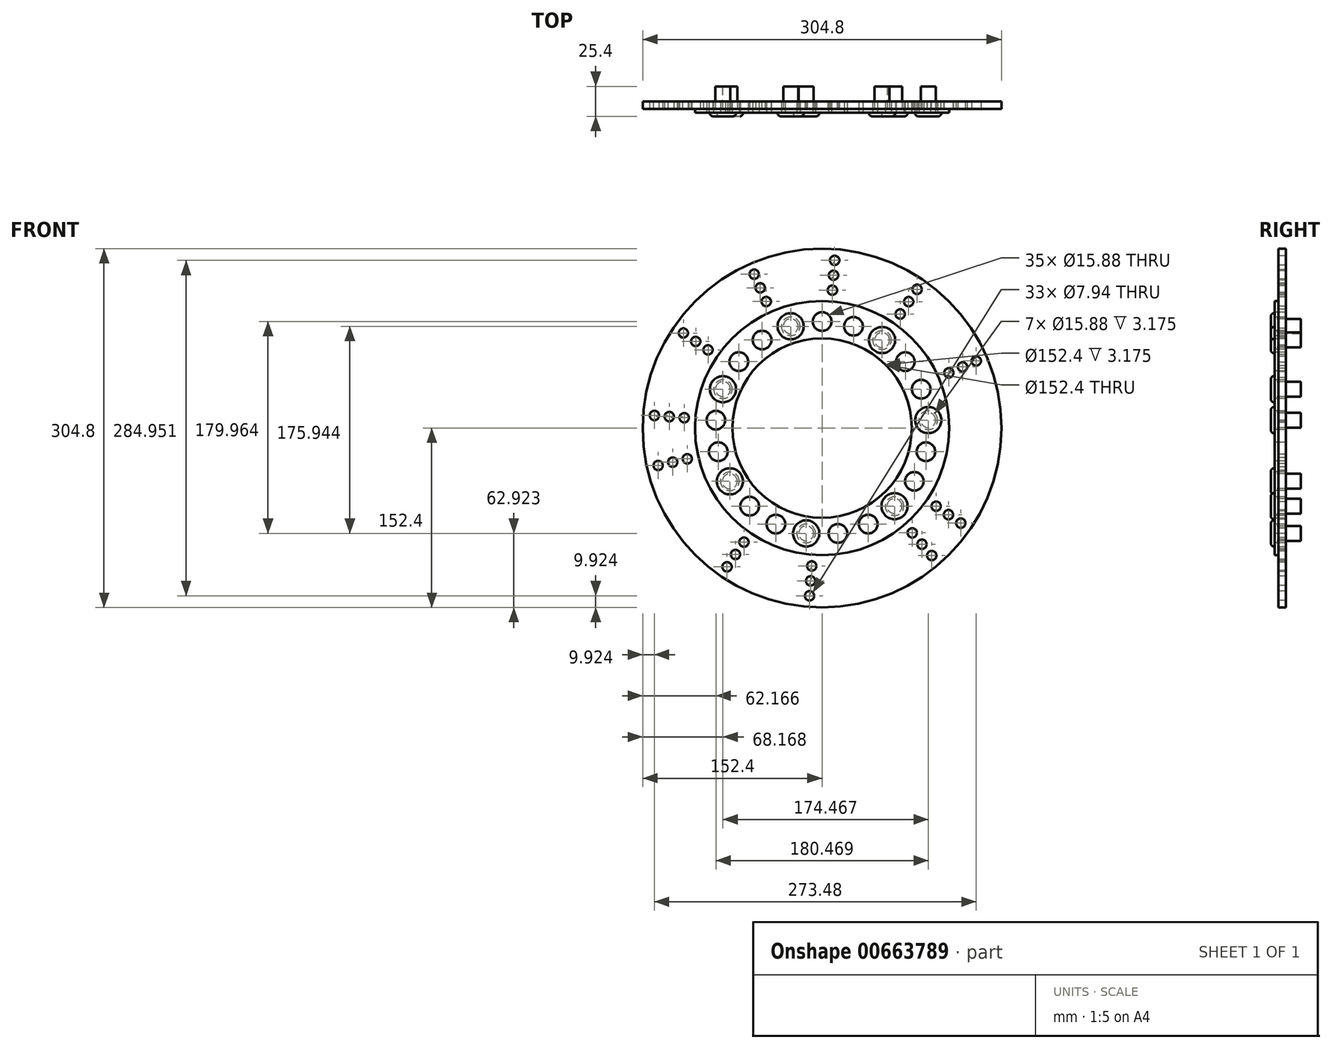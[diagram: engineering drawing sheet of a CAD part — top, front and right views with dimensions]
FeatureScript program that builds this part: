
annotation { "Feature Type Name" : "Feature", "Feature Type Description" : "" }
export const myFeature = defineFeature(function(context is Context, id is Id, definition is map)
    precondition{}
    {
        {
            var Q0;
            Q0=qCreatedBy(makeId("Front.planeOp"),FACE);
            var sketch = newSketch(context, id + "F0", { "sketchPlane" : qUnion([Q0])});
            skCircle(sketch, "E0", {"center": v(0, 0) * mm, "radius": 152.4 * mm});
            skCircle(sketch, "E1", {"center": v(0, 0) * mm, "radius": 76.2 * mm});
            skSolve(sketch);
        }
        {
            var Q0;
            Q0 = qSketchRegion(id + "F0", true);
            extrude(context, id + "F1", {"entities" : qUnion([Q0]), "depth" : 6.35 * mm, "offsetDistance" : 25.4 * mm});
        }
        {
            var Q0;
            Q0=makeQuery(id+"F1.opExtrude","CAP_FACE",FACE,{"disambiguationData":[OSD([sQuery(id+"F0.wireOp",EDGE,"E0"),sQuery(id+"F0.wireOp",EDGE,"E1")])],"isStart":false});
            var sketch = newSketch(context, id + "F2", { "sketchPlane" : qUnion([Q0])});
            skCircle(sketch, "E2", {"center": v(0, 0) * mm, "radius": 76.2 * mm});
            skCircle(sketch, "E3", {"center": v(0, 0) * mm, "radius": 107.95 * mm});
            skSolve(sketch);
        }
        {
            var Q0;
            Q0 = qSketchRegion(id + "F2", true);
            extrude(context, id + "F3", {"entities" : qUnion([Q0]), "depth" : 3.17 * mm, "offsetDistance" : 25.4 * mm});
        }
        {
            var Q0;
            Q0=makeQuery(id+"F3.opExtrude","CAP_FACE",FACE,{"disambiguationData":[OSD([sQuery(id+"F2.wireOp",EDGE,"E2"),sQuery(id+"F2.wireOp",EDGE,"E3")])],"isStart":false});
            var sketch = newSketch(context, id + "F4", { "sketchPlane" : qUnion([Q0])});
            skCircle(sketch, "E4", {"center": v(0, 90.49) * mm, "radius": 7.94 * mm});
            skCircle(sketch, "E5.1.0", {"center": v(-26.67, 86.47) * mm, "radius": 7.94 * mm});
            skCircle(sketch, "E5.2.0", {"center": v(-50.97, 74.76) * mm, "radius": 7.94 * mm});
            skCircle(sketch, "E5.3.0", {"center": v(-70.75, 56.42) * mm, "radius": 7.94 * mm});
            skCircle(sketch, "E5.4.0", {"center": v(-84.23, 33.06) * mm, "radius": 7.94 * mm});
            skCircle(sketch, "E5.5.0", {"center": v(-90.23, 6.76) * mm, "radius": 7.94 * mm});
            skCircle(sketch, "E5.6.0", {"center": v(-88.22, -20.14) * mm, "radius": 7.94 * mm});
            skCircle(sketch, "E5.7.0", {"center": v(-78.36, -45.24) * mm, "radius": 7.94 * mm});
            skCircle(sketch, "E5.8.0", {"center": v(-61.55, -66.33) * mm, "radius": 7.94 * mm});
            skCircle(sketch, "E5.9.0", {"center": v(-39.26, -81.53) * mm, "radius": 7.94 * mm});
            skCircle(sketch, "E5.10.0", {"center": v(-13.49, -89.48) * mm, "radius": 7.94 * mm});
            skCircle(sketch, "E5.11.0", {"center": v(13.49, -89.48) * mm, "radius": 7.94 * mm});
            skCircle(sketch, "E5.12.0", {"center": v(39.26, -81.53) * mm, "radius": 7.94 * mm});
            skCircle(sketch, "E5.13.0", {"center": v(61.55, -66.33) * mm, "radius": 7.94 * mm});
            skCircle(sketch, "E5.14.0", {"center": v(78.36, -45.24) * mm, "radius": 7.94 * mm});
            skCircle(sketch, "E5.15.0", {"center": v(88.22, -20.14) * mm, "radius": 7.94 * mm});
            skCircle(sketch, "E5.16.0", {"center": v(90.23, 6.76) * mm, "radius": 7.94 * mm});
            skCircle(sketch, "E5.17.0", {"center": v(84.23, 33.06) * mm, "radius": 7.94 * mm});
            skCircle(sketch, "E5.18.0", {"center": v(70.75, 56.42) * mm, "radius": 7.94 * mm});
            skCircle(sketch, "E5.19.0", {"center": v(50.97, 74.76) * mm, "radius": 7.94 * mm});
            skPoint(sketch, "E5.center", {"position": v(0, 0) * mm});
            skCircle(sketch, "E6.1.20.0", {"center": v(26.67, 86.47) * mm, "radius": 7.94 * mm});
            skSolve(sketch);
        }
        {
            var Q0;
            Q0 = qSketchRegion(id + "F4", true);
            extrude(context, id + "F5", {"entities" : qUnion([Q0]), "operationType" : NewBodyOperationType.REMOVE, "endBound" : BoundingType.THROUGH_ALL, "oppositeDirection" : true, "depth" : 25.4 * mm, "offsetDistance" : 25.4 * mm});
        }
        {
            var Q0;
            Q0=makeQuery(id+"F3.opExtrude","CAP_FACE",FACE,{"disambiguationData":[OSD([sQuery(id+"F2.wireOp",EDGE,"E2"),sQuery(id+"F2.wireOp",EDGE,"E3")])],"isStart":false});
            var sketch = newSketch(context, id + "F6", { "sketchPlane" : qUnion([Q0])});
            skCircle(sketch, "E7", {"center": v(-13.49, -89.48) * mm, "radius": 11.11 * mm});
            skCircle(sketch, "E8", {"center": v(-78.36, -45.24) * mm, "radius": 11.11 * mm});
            skCircle(sketch, "E9", {"center": v(-84.23, 33.06) * mm, "radius": 11.11 * mm});
            skCircle(sketch, "E10", {"center": v(-26.67, 86.47) * mm, "radius": 11.11 * mm});
            skCircle(sketch, "E11", {"center": v(50.97, 74.76) * mm, "radius": 11.11 * mm});
            skCircle(sketch, "E12", {"center": v(90.23, 6.76) * mm, "radius": 11.11 * mm});
            skCircle(sketch, "E13", {"center": v(61.55, -66.33) * mm, "radius": 11.11 * mm});
            skSolve(sketch);
        }
        {
            var Q0;
            Q0 = qSketchRegion(id + "F6", true);
            extrude(context, id + "F7", {"entities" : qUnion([Q0]), "operationType" : NewBodyOperationType.ADD, "depth" : 3.17 * mm, "offsetDistance" : 25.4 * mm});
        }
        {
            var Q0;
            Q0=makeQuery(id+"F1.opExtrude","CAP_FACE",FACE,{"disambiguationData":[OSD([sQuery(id+"F0.wireOp",EDGE,"E0"),sQuery(id+"F0.wireOp",EDGE,"E1")])],"isStart":false});
            var sketch = newSketch(context, id + "F8", { "sketchPlane" : qUnion([Q0])});
            skLineSegment(sketch, "E14", {"start": v(0, 107.95) * mm, "end": v(0, 152.4) * mm, "construction": true});
            skLineSegment(sketch, "E15", {"start": v(-7.94, 116.43) * mm, "end": v(7.94, 143.92) * mm, "construction": true});
            skCircle(sketch, "E16", {"center": v(0, 130.17) * mm, "radius": 3.97 * mm});
            skCircle(sketch, "E17", {"center": v(-7.94, 116.43) * mm, "radius": 3.97 * mm});
            skCircle(sketch, "E18", {"center": v(7.94, 143.92) * mm, "radius": 3.97 * mm});
            skCircle(sketch, "E19.1.0", {"center": v(-49.82, 120.27) * mm, "radius": 3.97 * mm});
            skCircle(sketch, "E19.1.1", {"center": v(-47.74, 136) * mm, "radius": 3.97 * mm});
            skCircle(sketch, "E19.1.2", {"center": v(-51.89, 104.53) * mm, "radius": 3.97 * mm});
            skCircle(sketch, "E19.2.0", {"center": v(-92.05, 92.05) * mm, "radius": 3.97 * mm});
            skCircle(sketch, "E19.2.1", {"center": v(-96.16, 107.38) * mm, "radius": 3.97 * mm});
            skCircle(sketch, "E19.2.2", {"center": v(-87.94, 76.71) * mm, "radius": 3.97 * mm});
            skCircle(sketch, "E19.3.0", {"center": v(-120.27, 49.82) * mm, "radius": 3.97 * mm});
            skCircle(sketch, "E19.3.1", {"center": v(-129.93, 62.41) * mm, "radius": 3.97 * mm});
            skCircle(sketch, "E19.3.2", {"center": v(-110.6, 37.22) * mm, "radius": 3.97 * mm});
            skCircle(sketch, "E19.4.0", {"center": v(-130.17, 0) * mm, "radius": 3.97 * mm});
            skCircle(sketch, "E19.4.1", {"center": v(-143.92, 7.94) * mm, "radius": 3.97 * mm});
            skCircle(sketch, "E19.4.2", {"center": v(-116.43, -7.94) * mm, "radius": 3.97 * mm});
            skCircle(sketch, "E19.5.0", {"center": v(-120.27, -49.82) * mm, "radius": 3.97 * mm});
            skCircle(sketch, "E19.5.1", {"center": v(-136, -47.74) * mm, "radius": 3.97 * mm});
            skCircle(sketch, "E19.5.2", {"center": v(-104.53, -51.89) * mm, "radius": 3.97 * mm});
            skCircle(sketch, "E19.6.0", {"center": v(-92.05, -92.05) * mm, "radius": 3.97 * mm});
            skCircle(sketch, "E19.6.1", {"center": v(-107.38, -96.16) * mm, "radius": 3.97 * mm});
            skCircle(sketch, "E19.6.2", {"center": v(-76.71, -87.94) * mm, "radius": 3.97 * mm});
            skCircle(sketch, "E19.7.0", {"center": v(-49.82, -120.27) * mm, "radius": 3.97 * mm});
            skCircle(sketch, "E19.7.1", {"center": v(-62.41, -129.93) * mm, "radius": 3.97 * mm});
            skCircle(sketch, "E19.7.2", {"center": v(-37.22, -110.6) * mm, "radius": 3.97 * mm});
            skCircle(sketch, "E19.8.0", {"center": v(0, -130.17) * mm, "radius": 3.97 * mm});
            skCircle(sketch, "E19.8.1", {"center": v(-7.94, -143.92) * mm, "radius": 3.97 * mm});
            skCircle(sketch, "E19.8.2", {"center": v(7.94, -116.43) * mm, "radius": 3.97 * mm});
            skCircle(sketch, "E19.9.0", {"center": v(49.82, -120.27) * mm, "radius": 3.97 * mm});
            skCircle(sketch, "E19.9.1", {"center": v(47.74, -136) * mm, "radius": 3.97 * mm});
            skCircle(sketch, "E19.9.2", {"center": v(51.89, -104.53) * mm, "radius": 3.97 * mm});
            skCircle(sketch, "E19.10.0", {"center": v(92.05, -92.05) * mm, "radius": 3.97 * mm});
            skCircle(sketch, "E19.10.1", {"center": v(96.16, -107.38) * mm, "radius": 3.97 * mm});
            skCircle(sketch, "E19.10.2", {"center": v(87.94, -76.71) * mm, "radius": 3.97 * mm});
            skCircle(sketch, "E19.11.0", {"center": v(120.27, -49.82) * mm, "radius": 3.97 * mm});
            skCircle(sketch, "E19.11.1", {"center": v(129.93, -62.41) * mm, "radius": 3.97 * mm});
            skCircle(sketch, "E19.11.2", {"center": v(110.6, -37.22) * mm, "radius": 3.97 * mm});
            skCircle(sketch, "E19.12.0", {"center": v(130.17, 0) * mm, "radius": 3.97 * mm});
            skCircle(sketch, "E19.12.1", {"center": v(143.92, -7.94) * mm, "radius": 3.97 * mm});
            skCircle(sketch, "E19.12.2", {"center": v(116.43, 7.94) * mm, "radius": 3.97 * mm});
            skCircle(sketch, "E19.13.0", {"center": v(120.27, 49.82) * mm, "radius": 3.97 * mm});
            skCircle(sketch, "E19.13.1", {"center": v(136, 47.74) * mm, "radius": 3.97 * mm});
            skCircle(sketch, "E19.13.2", {"center": v(104.53, 51.89) * mm, "radius": 3.97 * mm});
            skCircle(sketch, "E19.14.0", {"center": v(92.05, 92.05) * mm, "radius": 3.97 * mm});
            skCircle(sketch, "E19.14.1", {"center": v(107.38, 96.16) * mm, "radius": 3.97 * mm});
            skCircle(sketch, "E19.14.2", {"center": v(76.71, 87.94) * mm, "radius": 3.97 * mm});
            skCircle(sketch, "E19.15.0", {"center": v(49.82, 120.27) * mm, "radius": 3.97 * mm});
            skCircle(sketch, "E19.15.1", {"center": v(62.41, 129.93) * mm, "radius": 3.97 * mm});
            skCircle(sketch, "E19.15.2", {"center": v(37.22, 110.6) * mm, "radius": 3.97 * mm});
            skPoint(sketch, "E19.center", {"position": v(0, 0) * mm});
            skSolve(sketch);
        }
        {
            var Q0;
            Q0=makeQuery(id+"F7.opExtrude","CAP_FACE",FACE,{"disambiguationData":[OSD([sQuery(id+"F6.wireOp",EDGE,"E13")])],"isStart":false});
            var Q1;
            Q1=makeQuery(id+"F7.opExtrude","CAP_FACE",FACE,{"disambiguationData":[OSD([sQuery(id+"F6.wireOp",EDGE,"E7")])],"isStart":false});
            var Q2;
            Q2=makeQuery(id+"F7.opExtrude","CAP_FACE",FACE,{"disambiguationData":[OSD([sQuery(id+"F6.wireOp",EDGE,"E8")])],"isStart":false});
            var Q3;
            Q3=makeQuery(id+"F7.opExtrude","CAP_FACE",FACE,{"disambiguationData":[OSD([sQuery(id+"F6.wireOp",EDGE,"E9")])],"isStart":false});
            var Q4;
            Q4=makeQuery(id+"F7.opExtrude","CAP_FACE",FACE,{"disambiguationData":[OSD([sQuery(id+"F6.wireOp",EDGE,"E10")])],"isStart":false});
            var Q5;
            Q5=makeQuery(id+"F7.opExtrude","CAP_FACE",FACE,{"disambiguationData":[OSD([sQuery(id+"F6.wireOp",EDGE,"E11")])],"isStart":false});
            var Q6;
            Q6=makeQuery(id+"F7.opExtrude","CAP_FACE",FACE,{"disambiguationData":[OSD([sQuery(id+"F6.wireOp",EDGE,"E12")])],"isStart":false});
            fillet(context, id + "F9", {"entities" : qUnion([Q0, Q1, Q2, Q3, Q4, Q5, Q6]), "radius" : 2.54 * mm, "tangentPropagation" : true, "allowEdgeOverflow" : false});
        }
        {
            var Q0;
            Q0=makeQuery(id+"F7.opExtrude","CAP_FACE",FACE,{"disambiguationData":[OSD([sQuery(id+"F6.wireOp",EDGE,"E10")])],"isStart":false});
            var sketch = newSketch(context, id + "F10", { "sketchPlane" : qUnion([Q0])});
            skCircle(sketch, "E20", {"center": v(-26.67, 86.47) * mm, "radius": 6.35 * mm});
            skCircle(sketch, "E21.1.0", {"center": v(-84.23, 33.06) * mm, "radius": 6.35 * mm});
            skCircle(sketch, "E21.2.0", {"center": v(-78.36, -45.24) * mm, "radius": 6.35 * mm});
            skCircle(sketch, "E21.3.0", {"center": v(-13.49, -89.48) * mm, "radius": 6.35 * mm});
            skCircle(sketch, "E21.4.0", {"center": v(61.55, -66.33) * mm, "radius": 6.35 * mm});
            skCircle(sketch, "E21.5.0", {"center": v(90.23, 6.76) * mm, "radius": 6.35 * mm});
            skCircle(sketch, "E21.6.0", {"center": v(50.97, 74.76) * mm, "radius": 6.35 * mm});
            skPoint(sketch, "E21.center", {"position": v(0, 0) * mm});
            skSolve(sketch);
        }
        {
            var Q0;
            Q0 = qSketchRegion(id + "F10", true);
            extrude(context, id + "F11", {"entities" : qUnion([Q0]), "operationType" : NewBodyOperationType.ADD, "oppositeDirection" : true, "depth" : 25.4 * mm, "offsetDistance" : 25.4 * mm});
        }
        {
            var Q0;
            Q0=makeQuery(id+"F8.imprint","IMPRINT",FACE,{"disambiguationData":[TD([[makeQuery(id+"F8.imprint","IMPRINT",EDGE,{"derivedFrom":sQuery(id+"F8.wireOp",EDGE,"E16")}),-1.0]])]});
            var sketch = newSketch(context, id + "F12", { "sketchPlane" : qUnion([Q0])});
            skLineSegment(sketch, "E22", {"start": v(0, 0) * mm, "end": v(-57.68, 130.72) * mm, "construction": true});
            skLineSegment(sketch, "E23", {"start": v(0, 0) * mm, "end": v(-117.86, 80.77) * mm, "construction": true});
            skLineSegment(sketch, "E24", {"start": v(0, 0) * mm, "end": v(-142.48, 10.68) * mm, "construction": true});
            skLineSegment(sketch, "E25", {"start": v(0, 0) * mm, "end": v(-139.3, -31.8) * mm, "construction": true});
            skLineSegment(sketch, "E26", {"start": v(0, 0) * mm, "end": v(-80.77, -117.86) * mm, "construction": true});
            skLineSegment(sketch, "E27", {"start": v(0, 0) * mm, "end": v(-10.68, -142.48) * mm, "construction": true});
            skLineSegment(sketch, "E28", {"start": v(0, 0) * mm, "end": v(93.17, -108.31) * mm, "construction": true});
            skLineSegment(sketch, "E29", {"start": v(0, 0) * mm, "end": v(117.86, -80.77) * mm, "construction": true});
            skLineSegment(sketch, "E30", {"start": v(0, 0) * mm, "end": v(131, 57.02) * mm, "construction": true});
            skLineSegment(sketch, "E31", {"start": v(0, 0) * mm, "end": v(80.77, 117.86) * mm, "construction": true});
            skLineSegment(sketch, "E32", {"start": v(0, 0) * mm, "end": v(10.68, 142.48) * mm, "construction": true});
            skCircle(sketch, "E33", {"center": v(0, 0) * mm, "radius": 142.88 * mm, "construction": true});
            skCircle(sketch, "E34", {"center": v(0, 0) * mm, "radius": 130.18 * mm, "construction": true});
            skCircle(sketch, "E35", {"center": v(0, 0) * mm, "radius": 117.48 * mm, "construction": true});
            skCircle(sketch, "E36", {"center": v(10.68, 142.48) * mm, "radius": 3.97 * mm});
            skCircle(sketch, "E37", {"center": v(9.73, 129.81) * mm, "radius": 3.97 * mm});
            skCircle(sketch, "E38", {"center": v(8.78, 117.15) * mm, "radius": 3.97 * mm});
            skCircle(sketch, "E39", {"center": v(-47.42, 107.48) * mm, "radius": 3.97 * mm});
            skCircle(sketch, "E40", {"center": v(-52.55, 119.1) * mm, "radius": 3.97 * mm});
            skCircle(sketch, "E41", {"center": v(-57.68, 130.72) * mm, "radius": 3.97 * mm});
            skCircle(sketch, "E42", {"center": v(-96.9, 66.4) * mm, "radius": 3.97 * mm});
            skCircle(sketch, "E43", {"center": v(-107.38, 73.59) * mm, "radius": 3.97 * mm});
            skCircle(sketch, "E44", {"center": v(-117.86, 80.77) * mm, "radius": 3.97 * mm});
            skCircle(sketch, "E45", {"center": v(-142.48, 10.68) * mm, "radius": 3.97 * mm});
            skCircle(sketch, "E46", {"center": v(-129.81, 9.73) * mm, "radius": 3.97 * mm});
            skCircle(sketch, "E47", {"center": v(-117.15, 8.78) * mm, "radius": 3.97 * mm});
            skCircle(sketch, "E48", {"center": v(-139.3, -31.8) * mm, "radius": 3.97 * mm});
            skCircle(sketch, "E49", {"center": v(-126.91, -28.97) * mm, "radius": 3.97 * mm});
            skCircle(sketch, "E50", {"center": v(-114.53, -26.14) * mm, "radius": 3.97 * mm});
            skCircle(sketch, "E51", {"center": v(-80.77, -117.86) * mm, "radius": 3.97 * mm});
            skCircle(sketch, "E52", {"center": v(-73.59, -107.38) * mm, "radius": 3.97 * mm});
            skCircle(sketch, "E53", {"center": v(-66.4, -96.9) * mm, "radius": 3.97 * mm});
            skCircle(sketch, "E54", {"center": v(-10.68, -142.48) * mm, "radius": 3.97 * mm});
            skCircle(sketch, "E55", {"center": v(-9.73, -129.81) * mm, "radius": 3.97 * mm});
            skCircle(sketch, "E56", {"center": v(-8.78, -117.15) * mm, "radius": 3.97 * mm});
            skCircle(sketch, "E57", {"center": v(93.17, -108.31) * mm, "radius": 3.97 * mm});
            skCircle(sketch, "E58", {"center": v(84.9, -98.69) * mm, "radius": 3.97 * mm});
            skCircle(sketch, "E59", {"center": v(76.6, -89.06) * mm, "radius": 3.97 * mm});
            skCircle(sketch, "E60", {"center": v(117.86, -80.77) * mm, "radius": 3.97 * mm});
            skCircle(sketch, "E61", {"center": v(107.38, -73.59) * mm, "radius": 3.97 * mm});
            skCircle(sketch, "E62", {"center": v(96.9, -66.4) * mm, "radius": 3.97 * mm});
            skCircle(sketch, "E63", {"center": v(107.71, 46.88) * mm, "radius": 3.97 * mm});
            skCircle(sketch, "E64", {"center": v(119.36, 51.95) * mm, "radius": 3.97 * mm});
            skCircle(sketch, "E65", {"center": v(131, 57.02) * mm, "radius": 3.97 * mm});
            skCircle(sketch, "E66", {"center": v(66.4, 96.9) * mm, "radius": 3.97 * mm});
            skCircle(sketch, "E67", {"center": v(73.59, 107.38) * mm, "radius": 3.97 * mm});
            skCircle(sketch, "E68", {"center": v(80.77, 117.86) * mm, "radius": 3.97 * mm});
            skSolve(sketch);
        }
        {
            var Q0;
            Q0 = qSketchRegion(id + "F12", true);
            extrude(context, id + "F13", {"entities" : qUnion([Q0]), "operationType" : NewBodyOperationType.REMOVE, "endBound" : BoundingType.UP_TO_NEXT, "oppositeDirection" : true, "depth" : 25.4 * mm, "offsetDistance" : 25.4 * mm});
        }
    });
